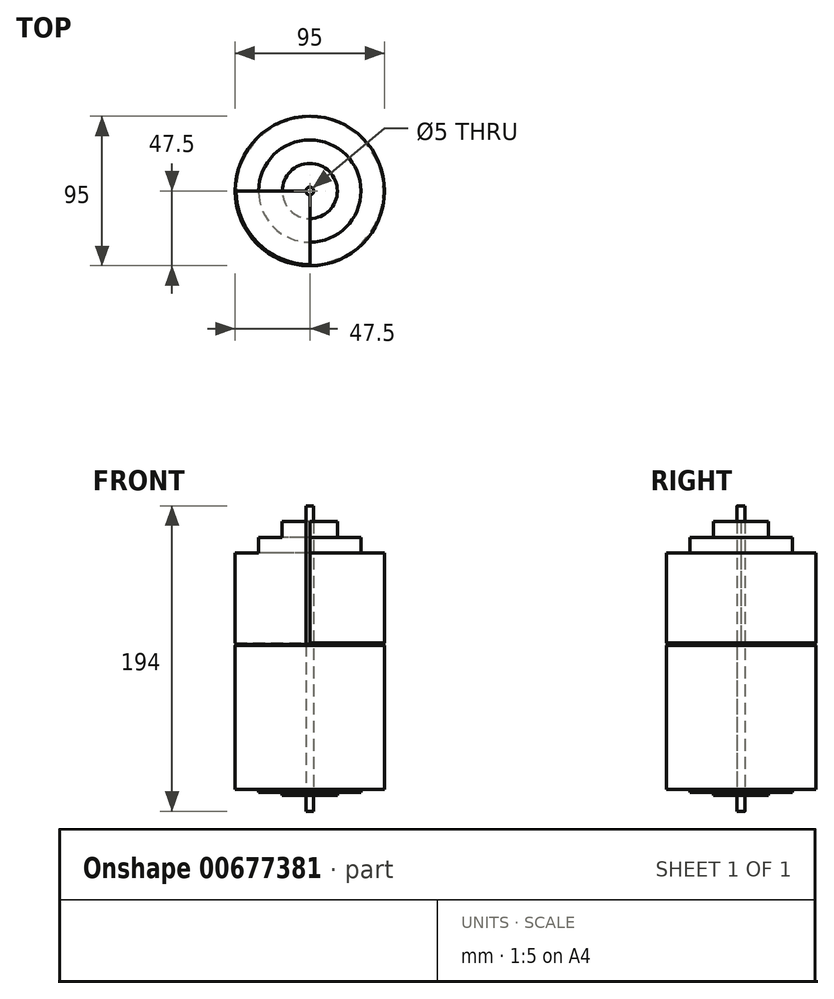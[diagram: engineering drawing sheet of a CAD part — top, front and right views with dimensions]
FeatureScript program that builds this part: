
annotation { "Feature Type Name" : "Feature", "Feature Type Description" : "" }
export const myFeature = defineFeature(function(context is Context, id is Id, definition is map)
    precondition{}
    {
        {
            var Q0;
            Q0=qCreatedBy(makeId("Top.planeOp"),FACE);
            cPlane(context, id + "F0", {"entities" : qUnion([Q0]), "cplaneType" : CPlaneType.OFFSET, "offset" : 80 * mm, "oppositeDirection" : true, "width" : 150 * mm, "height" : 150 * mm});
        }
        {
            var Q0;
            Q0=qCreatedBy(id+"F0.planeOp",FACE);
            var sketch = newSketch(context, id + "F1", { "sketchPlane" : qUnion([Q0])});
            skCircle(sketch, "E0", {"center": v(0, 0) * mm, "radius": 47.5 * mm});
            skCircle(sketch, "E1", {"center": v(0, 0) * mm, "radius": 32.5 * mm});
            skCircle(sketch, "E2", {"center": v(0, 0) * mm, "radius": 17.5 * mm});
            skCircle(sketch, "E3", {"center": v(0, 0) * mm, "radius": 2.5 * mm});
            skLineSegment(sketch, "E4", {"start": v(0, -47.5) * mm, "end": v(0, -2.5) * mm});
            skLineSegment(sketch, "E5", {"start": v(-47.5, 0) * mm, "end": v(-2.5, 0) * mm});
            skSolve(sketch);
        }
        {
            var Q0;
            Q0=qCreatedBy(makeId("Top.planeOp"),FACE);
            cPlane(context, id + "F2", {"entities" : qUnion([Q0]), "cplaneType" : CPlaneType.OFFSET, "offset" : 12 * mm, "width" : 150 * mm, "height" : 150 * mm});
        }
        {
            var Q0;
            Q0=qCreatedBy(makeId("Top.planeOp"),FACE);
            cPlane(context, id + "F3", {"entities" : qUnion([Q0]), "cplaneType" : CPlaneType.OFFSET, "offset" : 100 * mm, "width" : 150 * mm, "height" : 150 * mm});
        }
        {
            var Q0;
            Q0=qCreatedBy(id+"F3.planeOp",FACE);
            cPlane(context, id + "F4", {"entities" : qUnion([Q0]), "cplaneType" : CPlaneType.OFFSET, "offset" : 10 * mm, "oppositeDirection" : true, "width" : 150 * mm, "height" : 150 * mm});
        }
        {
            var Q0;
            Q0=qCreatedBy(id+"F4.planeOp",FACE);
            cPlane(context, id + "F5", {"entities" : qUnion([Q0]), "cplaneType" : CPlaneType.OFFSET, "offset" : 10 * mm, "oppositeDirection" : true, "width" : 150 * mm, "height" : 150 * mm});
        }
        {
            var Q0;
            Q0=qCreatedBy(id+"F5.planeOp",FACE);
            cPlane(context, id + "F6", {"entities" : qUnion([Q0]), "cplaneType" : CPlaneType.OFFSET, "offset" : 10 * mm, "oppositeDirection" : true, "width" : 150 * mm, "height" : 150 * mm});
        }
        {
            var Q0;
            {var subQ0=sQuery(id+"F1.wireOp",EDGE,"E4");var subQ1=sQuery(id+"F1.wireOp",EDGE,"E0");var subQ2=makeQuery(id+"F1.imprint","INTERSECT",VERTEX,{"derivedFrom":[subQ1,subQ0]});Q0=makeQuery(id+"F1.imprint","IMPRINT",FACE,{"disambiguationData":[TD([[makeQuery(id+"F1.imprint","IMPRINT",EDGE,{"disambiguationData":[TD([[subQ2,-1.0]])],"derivedFrom":subQ1}),1.0]])]});}
            var Q1;
            Q1=qCreatedBy(id+"F6.planeOp",FACE);
            extrude(context, id + "F7", {"entities" : qUnion([Q0]), "endBound" : BoundingType.UP_TO_SURFACE, "depth" : 25 * mm, "endBoundEntityFace" : qUnion([Q1]), "offsetDistance" : 25 * mm});
        }
        {
            var Q0;
            {var subQ0=sQuery(id+"F1.wireOp",EDGE,"E4");var subQ1=sQuery(id+"F1.wireOp",EDGE,"E0");var subQ2=makeQuery(id+"F1.imprint","INTERSECT",VERTEX,{"derivedFrom":[subQ1,subQ0]});Q0=makeQuery(id+"F1.imprint","IMPRINT",FACE,{"disambiguationData":[TD([[makeQuery(id+"F1.imprint","IMPRINT",EDGE,{"disambiguationData":[TD([[subQ2,1.0]])],"derivedFrom":subQ1}),1.0]])]});}
            var Q1;
            Q1=qCreatedBy(id+"F2.planeOp",FACE);
            extrude(context, id + "F8", {"entities" : qUnion([Q0]), "operationType" : NewBodyOperationType.ADD, "endBound" : BoundingType.UP_TO_SURFACE, "depth" : 25 * mm, "endBoundEntityFace" : qUnion([Q1]), "offsetDistance" : 25 * mm});
        }
        {
            var Q0;
            {var subQ0=sQuery(id+"F1.wireOp",EDGE,"E4");var subQ1=sQuery(id+"F1.wireOp",EDGE,"E1");var subQ2=makeQuery(id+"F1.imprint","INTERSECT",VERTEX,{"derivedFrom":[subQ1,subQ0]});Q0=makeQuery(id+"F1.imprint","IMPRINT",FACE,{"disambiguationData":[TD([[makeQuery(id+"F1.imprint","IMPRINT",EDGE,{"disambiguationData":[TD([[subQ2,1.0]])],"derivedFrom":subQ1}),1.0]])]});}
            var Q1;
            Q1=qCreatedBy(id+"F2.planeOp",FACE);
            extrude(context, id + "F9", {"entities" : qUnion([Q0]), "endBound" : BoundingType.UP_TO_SURFACE, "depth" : 25 * mm, "endBoundEntityFace" : qUnion([Q1]), "offsetDistance" : 25 * mm, "hasSecondDirection" : true, "secondDirectionOppositeDirection" : true, "secondDirectionDepth" : 2 * mm});
        }
        {
            var Q0;
            {var subQ0=sQuery(id+"F1.wireOp",EDGE,"E4");var subQ1=sQuery(id+"F1.wireOp",EDGE,"E1");var subQ2=makeQuery(id+"F1.imprint","INTERSECT",VERTEX,{"derivedFrom":[subQ1,subQ0]});Q0=makeQuery(id+"F1.imprint","IMPRINT",FACE,{"disambiguationData":[TD([[makeQuery(id+"F1.imprint","IMPRINT",EDGE,{"disambiguationData":[TD([[subQ2,-1.0]])],"derivedFrom":subQ1}),1.0]])]});}
            var Q1;
            Q1=qCreatedBy(id+"F5.planeOp",FACE);
            extrude(context, id + "F10", {"entities" : qUnion([Q0]), "operationType" : NewBodyOperationType.ADD, "endBound" : BoundingType.UP_TO_SURFACE, "depth" : 25 * mm, "endBoundEntityFace" : qUnion([Q1]), "offsetDistance" : 25 * mm, "hasSecondDirection" : true, "secondDirectionOppositeDirection" : true, "secondDirectionDepth" : 2 * mm});
        }
        {
            var Q0;
            {var subQ0=sQuery(id+"F1.wireOp",EDGE,"E4");var subQ1=sQuery(id+"F1.wireOp",EDGE,"E2");var subQ2=makeQuery(id+"F1.imprint","INTERSECT",VERTEX,{"derivedFrom":[subQ1,subQ0]});Q0=makeQuery(id+"F1.imprint","IMPRINT",FACE,{"disambiguationData":[TD([[makeQuery(id+"F1.imprint","IMPRINT",EDGE,{"disambiguationData":[TD([[subQ2,1.0]])],"derivedFrom":subQ1}),1.0]])]});}
            var Q1;
            Q1=qCreatedBy(id+"F2.planeOp",FACE);
            extrude(context, id + "F11", {"entities" : qUnion([Q0]), "endBound" : BoundingType.UP_TO_SURFACE, "depth" : 25 * mm, "endBoundEntityFace" : qUnion([Q1]), "offsetDistance" : 25 * mm, "hasSecondDirection" : true, "secondDirectionOppositeDirection" : true, "secondDirectionDepth" : 4 * mm});
        }
        {
            var Q0;
            {var subQ0=sQuery(id+"F1.wireOp",EDGE,"E4");var subQ1=sQuery(id+"F1.wireOp",EDGE,"E2");var subQ2=makeQuery(id+"F1.imprint","INTERSECT",VERTEX,{"derivedFrom":[subQ1,subQ0]});Q0=makeQuery(id+"F1.imprint","IMPRINT",FACE,{"disambiguationData":[TD([[makeQuery(id+"F1.imprint","IMPRINT",EDGE,{"disambiguationData":[TD([[subQ2,-1.0]])],"derivedFrom":subQ1}),1.0]])]});}
            var Q1;
            Q1=qCreatedBy(id+"F4.planeOp",FACE);
            extrude(context, id + "F12", {"entities" : qUnion([Q0]), "operationType" : NewBodyOperationType.ADD, "endBound" : BoundingType.UP_TO_SURFACE, "depth" : 25 * mm, "endBoundEntityFace" : qUnion([Q1]), "offsetDistance" : 25 * mm, "hasSecondDirection" : true, "secondDirectionOppositeDirection" : true, "secondDirectionDepth" : 4 * mm});
        }
        {
            var Q0;
            {var subQ0=sQuery(id+"F1.wireOp",EDGE,"E3");var subQ1=makeQuery(id+"F1.imprint","INTERSECT",VERTEX,{"derivedFrom":[subQ0,sQuery(id+"F1.wireOp",EDGE,"E4")]});Q0=makeQuery(id+"F1.imprint","IMPRINT",FACE,{"disambiguationData":[TD([[makeQuery(id+"F1.imprint","IMPRINT",EDGE,{"disambiguationData":[TD([[subQ1,1.0]])],"derivedFrom":subQ0}),1.0]])]});}
            var Q1;
            Q1=qCreatedBy(id+"F3.planeOp",FACE);
            extrude(context, id + "F13", {"entities" : qUnion([Q0]), "endBound" : BoundingType.UP_TO_SURFACE, "depth" : 25 * mm, "endBoundEntityFace" : qUnion([Q1]), "offsetDistance" : 25 * mm, "hasSecondDirection" : true, "secondDirectionOppositeDirection" : true, "secondDirectionDepth" : 14 * mm});
        }
        {
            var Q0;
            Q0=makeQuery(id+"F7.opExtrude","SWEPT_FACE",FACE,{"disambiguationData":[OSD([sQuery(id+"F1.wireOp",EDGE,"E5")])]});
            var sketch = newSketch(context, id + "F14", { "sketchPlane" : qUnion([Q0])});
            skLineSegment(sketch, "E6", {"start": v(-47.5, 12.8) * mm, "end": v(-46.7, 12) * mm});
            skLineSegment(sketch, "E7", {"start": v(-46.7, 12) * mm, "end": v(-47.5, 11.2) * mm});
            skLineSegment(sketch, "E8", {"start": v(47.5, 70) * mm, "end": v(47.5, -80) * mm, "construction": true});
            skLineSegment(sketch, "E9", {"start": v(-47.5, 12) * mm, "end": v(-47.5, 70) * mm, "construction": true});
            skLineSegment(sketch, "E10", {"start": v(-47.5, -80) * mm, "end": v(-47.5, 12) * mm, "construction": true});
            skLineSegment(sketch, "E11.0", {"start": v(-47.5, 12) * mm, "end": v(0, 12) * mm, "construction": true});
            skLineSegment(sketch, "E12", {"start": v(-47.5, 11.2) * mm, "end": v(-47.5, 12) * mm});
            skLineSegment(sketch, "E13", {"start": v(-47.5, 12.8) * mm, "end": v(-47.5, 12) * mm});
            skSolve(sketch);
        }
        {
            var Q0;
            Q0 = qSketchRegion(id + "F14", true);
            var Q1;
            {var subQ0=sQuery(id+"F1.wireOp",EDGE,"E0");Q1=makeQuery(id+"F8.boolean.opBoolean","MERGE",FACE,{"derivedFrom":[makeQuery(id+"F7.opExtrude","SWEPT_FACE",FACE,{"disambiguationData":[OSD([subQ0])]}),makeQuery(id+"F8.opExtrude","SWEPT_FACE",FACE,{"disambiguationData":[OSD([subQ0])]})]});}
            revolve(context, id + "F15", {"operationType" : NewBodyOperationType.REMOVE, "entities" : qUnion([Q0]), "axis" : qUnion([Q1]), "revolveType" : RevolveType.FULL, "oppositeDirection" : true});
        }
    });
